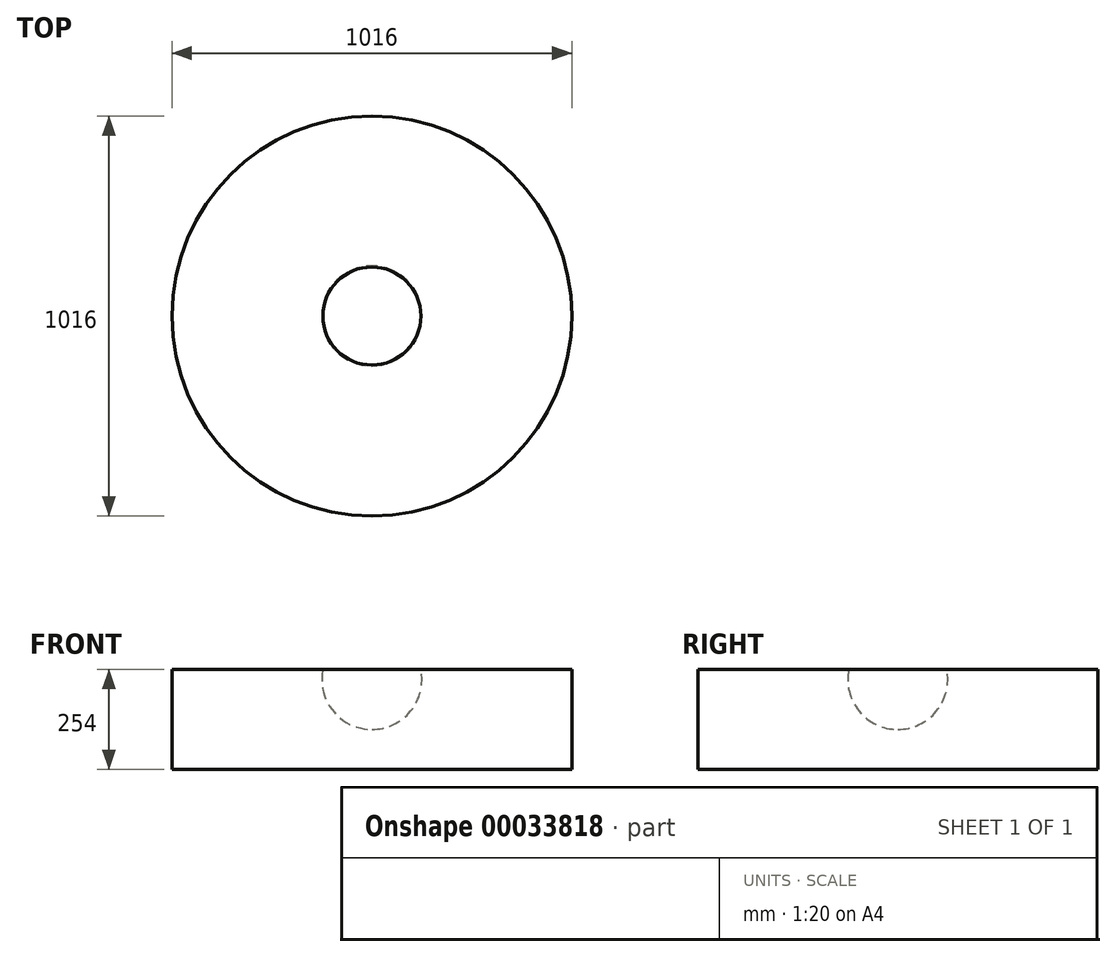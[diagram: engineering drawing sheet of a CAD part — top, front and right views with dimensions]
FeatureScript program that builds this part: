
annotation { "Feature Type Name" : "Feature", "Feature Type Description" : "" }
export const myFeature = defineFeature(function(context is Context, id is Id, definition is map)
    precondition{}
    {
        {
            var Q0;
            Q0=qCreatedBy(makeId("Front.planeOp"),FACE);
            var sketch = newSketch(context, id + "F0", { "sketchPlane" : qUnion([Q0])});
            skLineSegment(sketch, "E0.bottom", {"start": v(0, 0) * mm, "end": v(-508, 0) * mm});
            skLineSegment(sketch, "E0.top", {"start": v(-124.43, 254) * mm, "end": v(-508, 254) * mm});
            skLineSegment(sketch, "E0.left", {"start": v(0, 0) * mm, "end": v(0, 101.6) * mm});
            skLineSegment(sketch, "E0.right", {"start": v(-508, 0) * mm, "end": v(-508, 254) * mm});
            skArc(sketch, "E1", {"start": v(-124.43, 254) * mm, "mid": v(-98.37, 148.28) * mm, "end": v(0, 101.6) * mm});
            skPoint(sketch, "E2.orphan", {"position": v(0, 254) * mm});
            skSolve(sketch);
        }
        {
            var Q0;
            Q0=makeQuery(id+"F0.imprint","IMPRINT",FACE,{"disambiguationData":[TD([[makeQuery(id+"F0.imprint","IMPRINT",EDGE,{"derivedFrom":sQuery(id+"F0.wireOp",EDGE,"E0.bottom")}),-1.0]])]});
            var Q1;
            Q1=sQuery(id+"F0.wireOp",EDGE,"E0.left");
            revolve(context, id + "F1", {"entities" : qUnion([Q0]), "axis" : qUnion([Q1]), "revolveType" : RevolveType.FULL});
        }
    });
